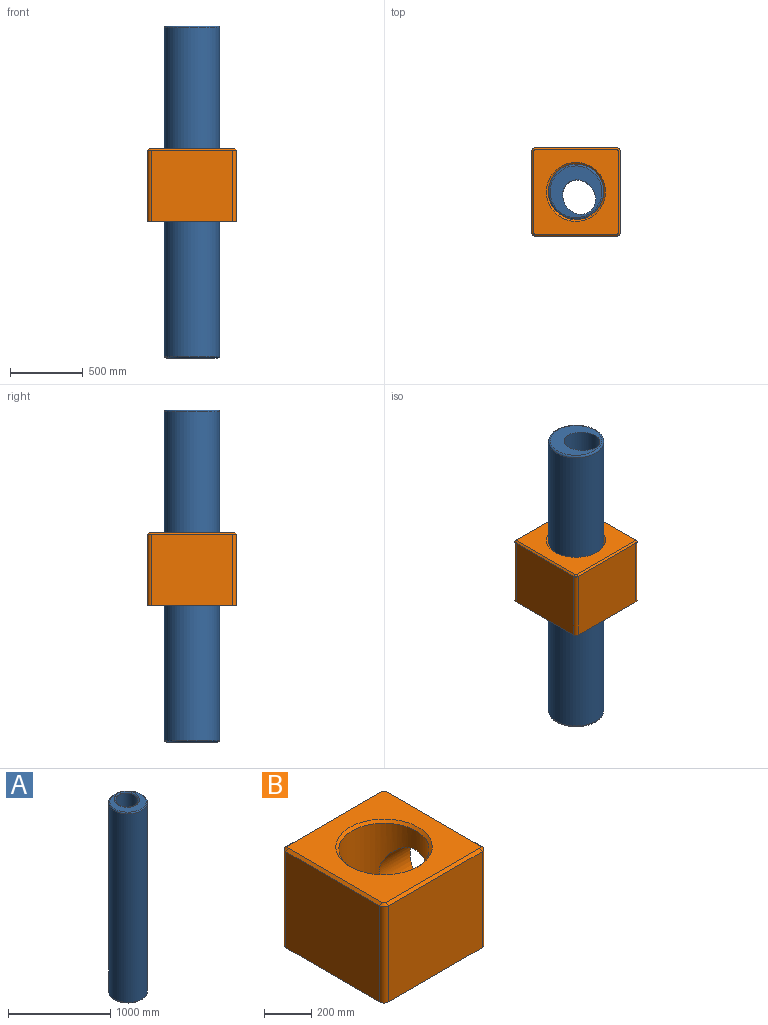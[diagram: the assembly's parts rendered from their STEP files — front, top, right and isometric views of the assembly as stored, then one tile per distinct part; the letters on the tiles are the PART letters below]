
ASSEMBLY  parts=2 mates=1
PART A: 7 faces, bbox 412.4x412.4x2286 mm
  f0: cylinder r=190.5mm len=2260.6mm, axis (0,0,-1), area 2705817.9mm2, adj f4,f6
  f1: plane 355.6x355.6mm, normal (0,0,1), area 47212.4mm2, adj f4,f5
  f2: plane 355.6x355.6mm, normal (0,0,-1), area 56941.2mm2, adj f3,f6
  f3: extruded ~2273.3x238.83mm, area 1664286.6mm2, adj f2,f5
  f4: torus R=177.8mm, axis (0,0,1), area 23262.8mm2, adj f0,f1,f5
  f5: bspline ~264.87x252.39mm, area 15184.1mm2, adj f1,f3,f4
  f6: torus R=177.8mm, axis (0,0,1), area 23299.6mm2, adj f0,f2
PART B: 21 faces, bbox 609.6x609.6x508 mm
  f0: cylinder r=25.4mm len=495.3mm, axis (0,0,-1), area 19761.6mm2, adj f1,f8,f10,f12
  f1: plane 558.8x495.3mm, normal (-1,0,0), area 276773.6mm2, adj f0,f2,f10,f14
  f2: cylinder r=25.4mm len=495.3mm, axis (0,0,-1), area 19761.6mm2, adj f1,f3,f10,f16
  f3: plane 558.8x495.3mm, normal (0,-1,0), area 276773.6mm2, adj f2,f4,f10,f18
  f4: cylinder r=25.4mm len=495.3mm, axis (0,0,-1), area 19761.6mm2, adj f3,f5,f10,f17
  f5: plane 558.8x495.3mm, normal (1,0,0), area 207408.8mm2, adj f4,f6,f10,f15,f20
  f6: cylinder r=25.4mm len=495.3mm, axis (0,0,-1), area 19761.6mm2, adj f5,f8,f10,f13
  f7: cylinder r=190.5mm len=495.3mm, axis (0,0,-1), area 516373.2mm2, adj f10,f19,f20
  f8: plane 558.8x495.3mm, normal (0,1,0), area 276773.6mm2, adj f0,f6,f10,f11
  f9: plane 584.2x584.2mm, normal (0,0,1), area 211434.1mm2, adj f11,f12,f13,f14,f15,f16,f17,f18
  f10: plane 609.6x609.6mm, normal (0,0,-1), area 257049.2mm2, adj f0,f1,f2,f3,f4,f5,f6,f7
  f11: plane 558.8x12.7mm, normal (0,0.71,0.71), area 10036.3mm2, adj f8,f9,f12,f13
  f12: cone r=12.7mm half-angle=45deg, axis (0,0,-1), area 537.4mm2, adj f0,f9,f11,f14
  f13: cone r=12.7mm half-angle=45deg, axis (0,0,-1), area 537.4mm2, adj f6,f9,f11,f15
  f14: plane 558.8x12.7mm, normal (-0.71,0,0.71), area 10036.3mm2, adj f1,f9,f12,f16
  f15: plane 558.8x12.7mm, normal (0.71,0,0.71), area 10036.3mm2, adj f5,f9,f13,f17
  f16: cone r=12.7mm half-angle=45deg, axis (0,0,-1), area 537.4mm2, adj f2,f9,f14,f18
  f17: cone r=12.7mm half-angle=45deg, axis (0,0,-1), area 537.4mm2, adj f4,f9,f15,f18
  f18: plane 558.8x12.7mm, normal (0,-0.71,0.71), area 10036.3mm2, adj f3,f9,f16,f17
  f19: cone r=190.5mm half-angle=45deg, axis (0,0,1), area 22214.4mm2, adj f7,f9
  f20: cylinder r=148.59mm len=297.18mm, axis (1,0,0), area 138071.1mm2, adj f5,f7
PLACE A rot(axis=(1,0,0),180deg) t=(-590.88,-1100.8,2563.81)mm
PLACE B t=(-590.88,-1100.8,1214.35)mm
MATE slider A.f0 <-> B.f7  axis (0,0,-1) through (-590.88,-1100.8,277.81)mm
